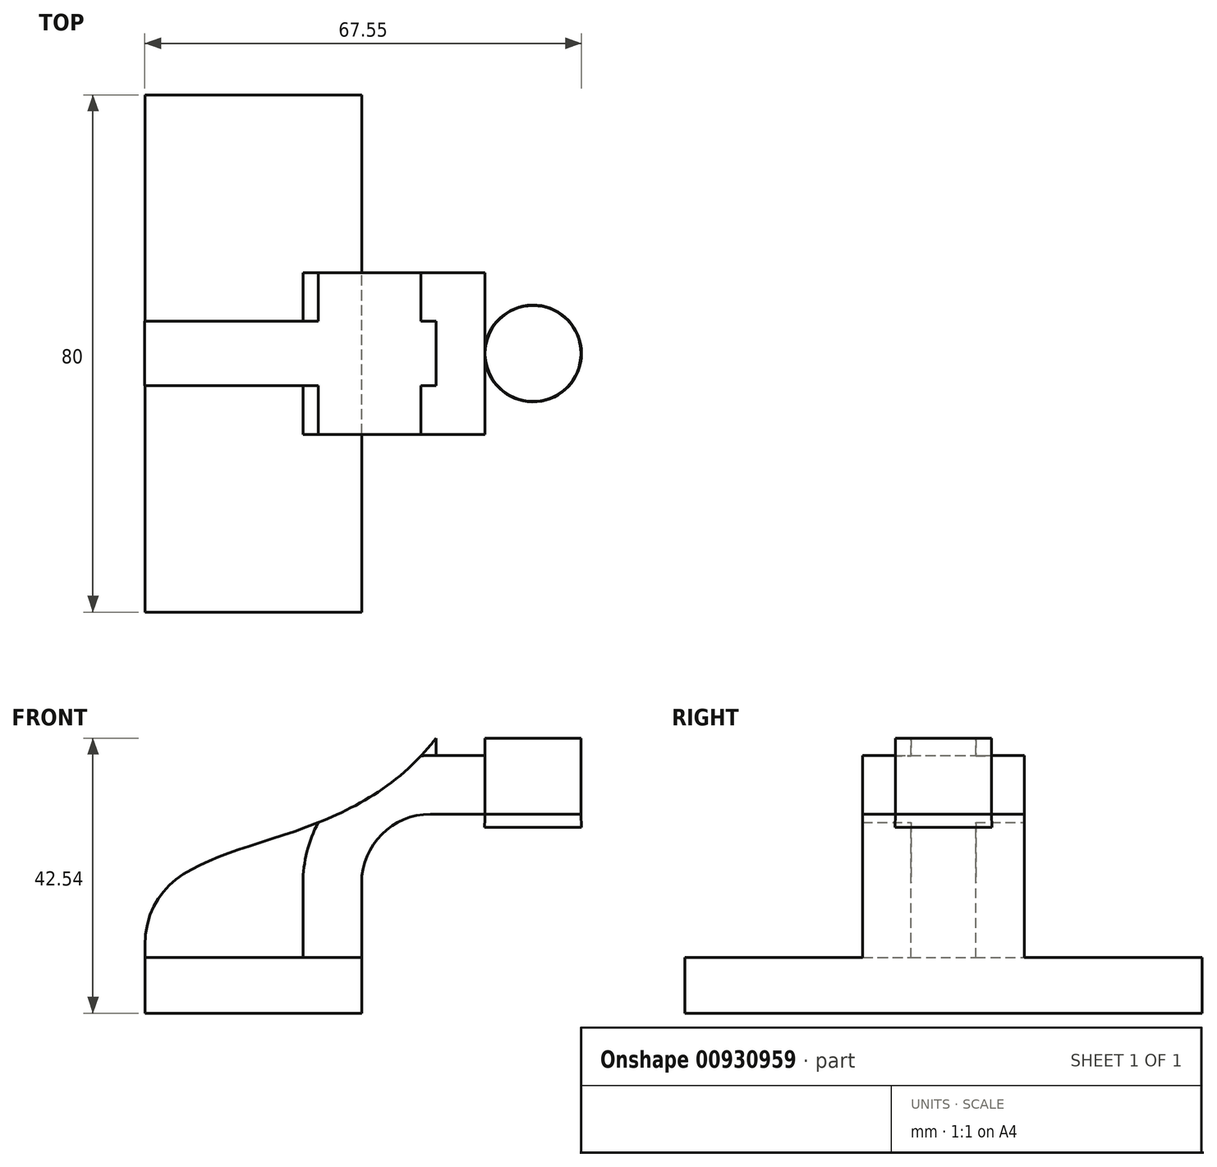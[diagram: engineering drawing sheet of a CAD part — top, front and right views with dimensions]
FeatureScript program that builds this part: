
annotation { "Feature Type Name" : "Feature", "Feature Type Description" : "" }
export const myFeature = defineFeature(function(context is Context, id is Id, definition is map)
    precondition{}
    {
        {
            var Q0;
            Q0=qCreatedBy(makeId("Front.planeOp"),FACE);
            var sketch = newSketch(context, id + "F0", { "sketchPlane" : qUnion([Q0])});
            skLineSegment(sketch, "E0.bottom", {"start": v(16.75, -4.3) * mm, "end": v(-16.75, -4.3) * mm});
            skLineSegment(sketch, "E0.top", {"start": v(16.75, 4.3) * mm, "end": v(-16.75, 4.3) * mm});
            skLineSegment(sketch, "E0.left", {"start": v(16.75, -4.3) * mm, "end": v(16.75, 4.3) * mm});
            skLineSegment(sketch, "E0.right", {"start": v(-16.75, -4.3) * mm, "end": v(-16.75, 4.3) * mm});
            skPoint(sketch, "E0.middle", {"position": v(0, 0) * mm});
            skLineSegment(sketch, "E1.bottom", {"start": v(43.26, 24.44) * mm, "end": v(28.26, 24.44) * mm});
            skLineSegment(sketch, "E1.top", {"start": v(43.26, 38.24) * mm, "end": v(28.26, 38.24) * mm});
            skLineSegment(sketch, "E1.left", {"start": v(43.26, 24.44) * mm, "end": v(43.26, 38.24) * mm});
            skLineSegment(sketch, "E1.right", {"start": v(28.26, 24.44) * mm, "end": v(28.26, 38.24) * mm});
            skPoint(sketch, "E1.middle", {"position": v(35.76, 31.34) * mm});
            skLineSegment(sketch, "E2", {"start": v(16.75, 4.3) * mm, "end": v(16.75, 15.84) * mm});
            skArc(sketch, "E3", {"start": v(16.75, 15.84) * mm, "mid": v(19.87, 23.37) * mm, "end": v(27.4, 26.48) * mm});
            skLineSegment(sketch, "E4", {"start": v(27.4, 26.48) * mm, "end": v(35.85, 26.48) * mm});
            skLineSegment(sketch, "E5.0", {"start": v(27.4, 35.55) * mm, "end": v(35.85, 35.55) * mm});
            skArc(sketch, "E5.1", {"start": v(7.69, 15.84) * mm, "mid": v(13.46, 29.78) * mm, "end": v(27.4, 35.55) * mm});
            skLineSegment(sketch, "E5.2", {"start": v(7.69, 4.3) * mm, "end": v(7.69, 15.84) * mm});
            skLineSegment(sketch, "E6", {"start": v(35.76, 24.44) * mm, "end": v(35.85, 26.48) * mm});
            skLineSegment(sketch, "E7", {"start": v(35.85, 35.55) * mm, "end": v(35.85, 26.48) * mm});
            skLineSegment(sketch, "E8", {"start": v(35.85, 35.55) * mm, "end": v(35.85, 38.24) * mm});
            skFitSpline(sketch, "E9", {"points": [v(-16.75, 4.3) * mm, v(28.26, 38.24) * mm], "startDerivative": vector(-3.94, 65.74) * mm, "endDerivative": vector(49.5, 64.43) * mm});
            skSolve(sketch);
        }
        {
            var Q0;
            {var subQ1=sQuery(id+"F0.wireOp",EDGE,"E2");Q0=makeQuery(id+"F0.imprint","IMPRINT",FACE,{"disambiguationData":[TD([[makeQuery(id+"F0.imprint","IMPRINT",EDGE,{"derivedFrom":subQ1}),1.0]])]});}
            var Q1;
            {var subQ5=sQuery(id+"F0.wireOp",EDGE,"E7");Q1=makeQuery(id+"F0.imprint","IMPRINT",FACE,{"disambiguationData":[TD([[makeQuery(id+"F0.imprint","IMPRINT",EDGE,{"derivedFrom":subQ5}),-1.0]])]});}
            extrude(context, id + "F1", {"entities" : qUnion([Q0, Q1]), "endBound" : BoundingType.SYMMETRIC, "depth" : 25 * mm, "offsetDistance" : 25 * mm});
        }
        {
            var Q0;
            Q0=makeQuery(id+"F0.imprint","IMPRINT",FACE,{"disambiguationData":[TD([[makeQuery(id+"F0.imprint","IMPRINT",EDGE,{"derivedFrom":sQuery(id+"F0.wireOp",EDGE,"E0.bottom")}),-1.0]])]});
            extrude(context, id + "F2", {"entities" : qUnion([Q0]), "operationType" : NewBodyOperationType.ADD, "endBound" : BoundingType.SYMMETRIC, "depth" : 80 * mm, "offsetDistance" : 25 * mm});
        }
        {
            var Q0;
            {var subQ1=sQuery(id+"F0.wireOp",EDGE,"E1.left");Q0=makeQuery(id+"F0.imprint","IMPRINT",FACE,{"disambiguationData":[TD([[makeQuery(id+"F0.imprint","IMPRINT",EDGE,{"derivedFrom":subQ1}),1.0]])]});}
            var Q1;
            Q1=sQuery(id+"F0.wireOp",EDGE,"E1.left");
            revolve(context, id + "F3", {"operationType" : NewBodyOperationType.ADD, "surfaceOperationType" : NewSurfaceOperationType.NEW, "entities" : qUnion([Q0]), "axis" : qUnion([Q1]), "revolveType" : RevolveType.FULL});
        }
        {
            var Q0;
            {var subQ3=sQuery(id+"F0.wireOp",EDGE,"E5.2");Q0=makeQuery(id+"F0.imprint","IMPRINT",FACE,{"disambiguationData":[TD([[makeQuery(id+"F0.imprint","IMPRINT",EDGE,{"derivedFrom":subQ3}),1.0]])]});}
            var Q1;
            {var subQ0=sQuery(id+"F0.wireOp",EDGE,"E9");var subQ1=sQuery(id+"F0.wireOp",EDGE,"E5.1");var subQ2=makeQuery(id+"F0.imprint","INTERSECT",VERTEX,{"disambiguationData":[OD(0.0)],"derivedFrom":[subQ1,subQ0]});Q1=makeQuery(id+"F0.imprint","IMPRINT",FACE,{"disambiguationData":[TD([[makeQuery(id+"F0.imprint","IMPRINT",EDGE,{"disambiguationData":[TD([[subQ2,-1.0]])],"derivedFrom":subQ1}),-1.0]])]});}
            var Q2;
            {var subQ3=sQuery(id+"F0.wireOp",EDGE,"E5.0");var subQ5=sQuery(id+"F0.wireOp",EDGE,"E5.1");var subQ6=makeQuery(id+"F0.imprint","INTERSECT",VERTEX,{"derivedFrom":[subQ3,subQ5]});Q2=makeQuery(id+"F0.imprint","IMPRINT",FACE,{"disambiguationData":[TD([[makeQuery(id+"F0.imprint","IMPRINT",EDGE,{"disambiguationData":[TD([[subQ6,-1.0]])],"derivedFrom":subQ3}),1.0]])]});}
            extrude(context, id + "F4", {"entities" : qUnion([Q0, Q1, Q2]), "operationType" : NewBodyOperationType.ADD, "endBound" : BoundingType.SYMMETRIC, "depth" : 10 * mm, "offsetDistance" : 25 * mm});
        }
    });
